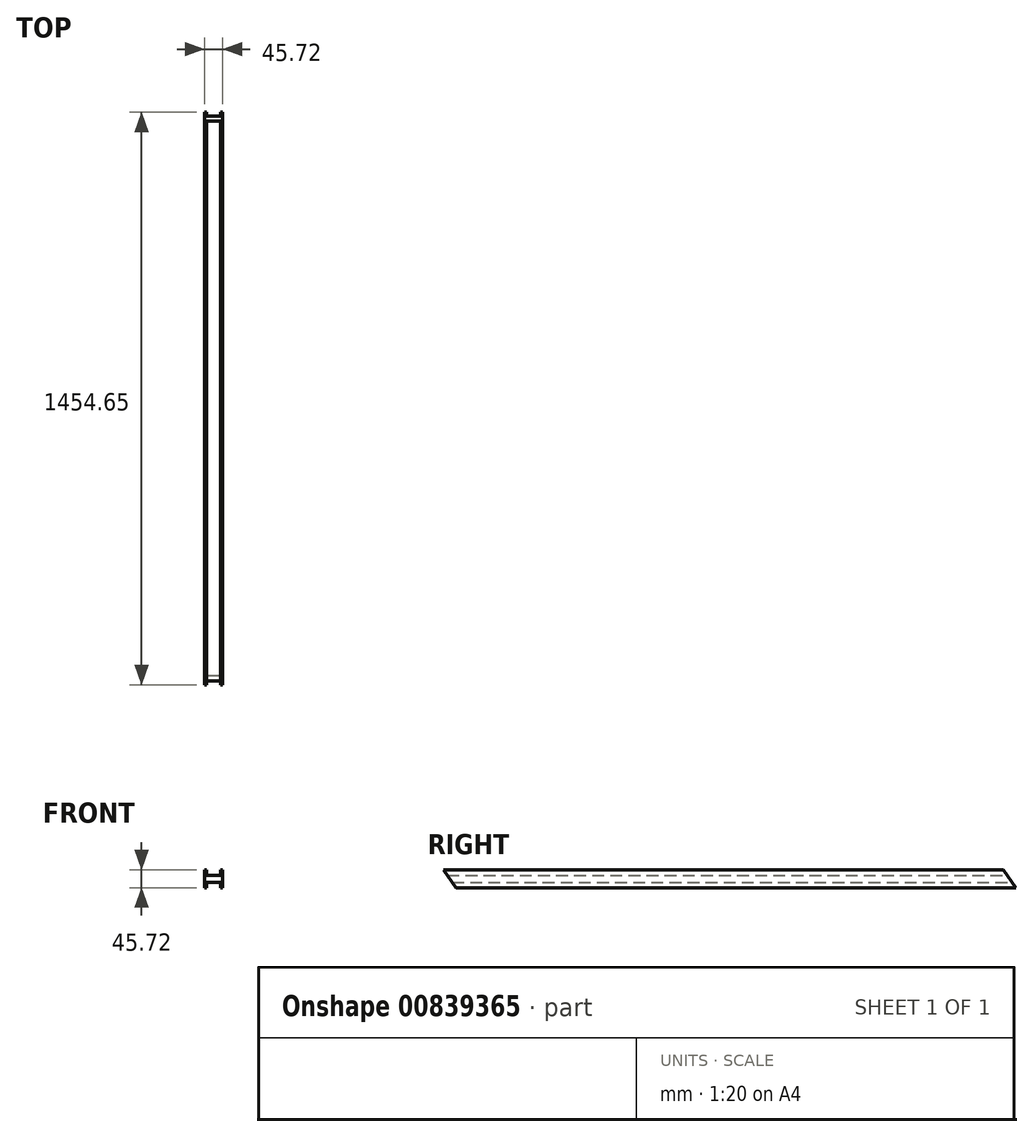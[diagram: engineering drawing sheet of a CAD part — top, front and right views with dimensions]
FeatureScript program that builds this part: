
annotation { "Feature Type Name" : "Feature", "Feature Type Description" : "" }
export const myFeature = defineFeature(function(context is Context, id is Id, definition is map)
    precondition{}
    {
        {
            var Q0;
            Q0=qCreatedBy(makeId("Front.planeOp"),FACE);
            var sketch = newSketch(context, id + "F0", { "sketchPlane" : qUnion([Q0])});
            skLineSegment(sketch, "E0.bottom", {"start": v(22.86, 22.86) * mm, "end": v(17.8, 22.86) * mm});
            skLineSegment(sketch, "E0.top", {"start": v(22.86, -22.86) * mm, "end": v(17.8, -22.86) * mm});
            skLineSegment(sketch, "E0.left", {"start": v(22.86, 22.86) * mm, "end": v(22.86, -22.86) * mm});
            skLineSegment(sketch, "E0.right", {"start": v(-22.86, 22.86) * mm, "end": v(-22.86, -22.86) * mm});
            skPoint(sketch, "E0.middle", {"position": v(0, 0) * mm});
            skLineSegment(sketch, "E1.top", {"start": v(-18.22, 8.64) * mm, "end": v(17.8, 8.64) * mm});
            skLineSegment(sketch, "E1.left", {"start": v(-18.22, 22.86) * mm, "end": v(-18.22, 8.64) * mm});
            skLineSegment(sketch, "E1.right", {"start": v(17.8, 22.86) * mm, "end": v(17.8, 8.64) * mm});
            skLineSegment(sketch, "E2", {"start": v(-65.42, 0) * mm, "end": v(65.2, 0) * mm, "construction": true});
            skLineSegment(sketch, "E3.MirrorCS", {"start": v(-18.22, -22.86) * mm, "end": v(-18.22, -8.64) * mm});
            skLineSegment(sketch, "E4.MirrorCS", {"start": v(-18.22, -8.64) * mm, "end": v(17.8, -8.64) * mm});
            skLineSegment(sketch, "E5.MirrorCS", {"start": v(17.8, -22.86) * mm, "end": v(17.8, -8.64) * mm});
            skLineSegment(sketch, "E6.trimOffspring", {"start": v(-18.22, 22.86) * mm, "end": v(-22.86, 22.86) * mm});
            skPoint(sketch, "E7.orphan", {"position": v(17.8, -31.29) * mm});
            skLineSegment(sketch, "E8.trimOffspring", {"start": v(-18.22, -22.86) * mm, "end": v(-22.86, -22.86) * mm});
            skPoint(sketch, "E9.orphan", {"position": v(-18.22, -31.29) * mm});
            skSolve(sketch);
        }
        {
            var Q0;
            Q0=qSketchRegion(id+"F0",true);
            extrude(context, id + "F1", {"entities" : qUnion([Q0]), "endBound" : BoundingType.SYMMETRIC, "depth" : 1695.45 * mm, "offsetDistance" : 25.4 * mm});
        }
        {
            var Q0;
            Q0=makeQuery(id+"F1.opExtrude","SWEPT_FACE",FACE,{"disambiguationData":[OSD([sQuery(id+"F0.wireOp",EDGE,"E0.left")])]});
            var sketch = newSketch(context, id + "F2", { "sketchPlane" : qUnion([Q0])});
            skLineSegment(sketch, "E10", {"start": v(-847.73, 366.76) * mm, "end": v(-847.73, -22.86) * mm});
            skLineSegment(sketch, "E11", {"start": v(-847.73, -22.86) * mm, "end": v(-574.9, -22.86) * mm});
            skLineSegment(sketch, "E12", {"start": v(-574.9, -22.86) * mm, "end": v(-847.73, 366.76) * mm});
            skLineSegment(sketch, "E13", {"start": v(847.73, -22.86) * mm, "end": v(815.71, 22.86) * mm});
            skLineSegment(sketch, "E14", {"start": v(815.71, 22.86) * mm, "end": v(847.73, 22.86) * mm});
            skLineSegment(sketch, "E15", {"start": v(847.73, 22.86) * mm, "end": v(847.73, -22.86) * mm});
            skSolve(sketch);
        }
        {
            var Q0;
            Q0 = qSketchRegion(id + "F2", true);
            extrude(context, id + "F3", {"entities" : qUnion([Q0]), "operationType" : NewBodyOperationType.REMOVE, "endBound" : BoundingType.THROUGH_ALL, "oppositeDirection" : true, "depth" : 25.4 * mm, "offsetDistance" : 25.4 * mm});
        }
    });
